# Revit family: Радиатор_текущ_2
name_source: partatom
category: Оборудование
revit_build: Autodesk Revit 2017 (Build: 20160225_1515(x64)
units: mm (PartAtom-declared; Revit-internal decimal feet)

## family parameters
Всегда вертикально = Да
Заголовок OmniClass = Climate Control (HVAC)
На основе рабочей плоскости = Нет
Номер OmniClass = 23.75.00.00
Общий = Нет
При загрузке вырезать с полостями = Нет
Размер круглого соединителя = Использовать диаметр
Тип детали = Нормальный
Точка расчета площади = Нет

## types (11) — shared parameters
Единица измерения = шт.

## per-type parameters (varying)
| type | ASDK_int | ASDK_out |
| 4 | -273 °C | -273 °C |
| 5 | -273 °C | -273 °C |
| 6 | 95 °C | 70 °C |
| 7 | -273 °C | -273 °C |
| 8 | -273 °C | -273 °C |
| 9 | -273 °C | -273 °C |
| 10 | -273 °C | -273 °C |
| 11 | -273 °C | -273 °C |
| 12 | -273 °C | -273 °C |
| 13 | -273 °C | -273 °C |
| 14 | -273 °C | -273 °C |

## geometry (parser evidence)
native form markers: Blend x2
no freeform markers — native parametric forms only
